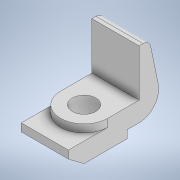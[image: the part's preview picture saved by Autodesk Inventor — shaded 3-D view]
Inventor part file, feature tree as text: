
AUTODESK INVENTOR PART (.ipt)
format: ipt  version: 2022.2 (Build 262287030, 287C)  size: 139,776 bytes
history: native  units: in
note: dims shown in document units (in); Inventor stores cm internally (conversion verified against a paired STEP export)
features: sketch x3, extrude x2, hole x1
ambient origin geometry x8: Origin, YZ Plane, XZ Plane, XY Plane, X Axis, Y Axis, Z Axis, Center Point
bodies: Solid1 (feature_tree)
feature tree (6):
  extrude  "Extrusion1"  Depth=4.75in
  extrude  "Extrusion2"  Depth=1.25in
  hole  "Hole1"  [1 undecoded]
  sketch  "Sketch1"  dims[d0=4.75in d1=2.75in]
  sketch  "Sketch2"  dims[d2=1.25in d3=1.25in]
  sketch  "Sketch3"  dims[d4=0.5in d5=0.25in d6=3.0in d7=0.5in d8=0.5in d9=4.5in d10=2.0in d11=0.75in d12=0.0in d13=3.0in d14=0.0in d15=1.5in d16=1.0in d17=0.0in d18=1.5in d19=0.75in d20=0.375in d21=0.25in d22=0.5635in d23=1.0in d24=0.8108in]
note: 1 required parameter value undecoded (feature->parameter linkage not recoverable at this tier; creation-order binding heuristic only, values carry confidence <= 0.55)
